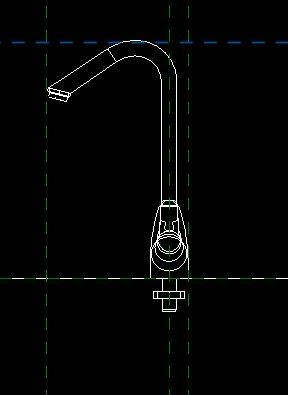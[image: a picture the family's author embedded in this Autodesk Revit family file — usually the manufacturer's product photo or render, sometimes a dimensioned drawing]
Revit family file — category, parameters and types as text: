
# Revit family: AV5030001_Grifería para Lavaplatos Sencillo Aluvia Palanca
name_source: partatom
category: Plumbing Fixtures
units: mm (PartAtom-declared; Revit-internal decimal feet)

## family parameters
Cut with Voids When Loaded = No
Host = Face
OmniClass Number = 23.45.55.14
OmniClass Title = Single Faucets
Part Type = Normal
Room Calculation Point = No
Round Connector Dimension = Use Diameter
Shared = No

## types (1)
- AV5030001_Grifería para Lavaplatos Sencillo Aluvia Palanca
    Alto = 333 mm  [stored 1.09252 ft]
    Ancho = 103 mm  [stored 0.337927 ft]
    Capacidad de flujo máximo a 60 psi = 5,7 L/min
    Default Elevation = 1219 mm
    Fabricante = Corona
    Garantia = 30 años
    Material = Corona_Plastico_Cromado
    Normatividad NTC 1644 = SI
    Peso Neto = 282 gr. - 0,62 lb
    Profundidad = 200 mm  [stored 0.656168 ft]
    Temperatura de uso = 5ºC a 71ºC
    URL = https://corona.co
    Vida útil o desgaste (pico) = 50.000 ciclos
    Vida útil o desgaste (unidad) = 500.000 ciclos

note: [stored X ft] marks values corroborated as IEEE doubles in the binary element streams (Revit-internal decimal feet)

## geometry (parser evidence)
native form markers: Sweep x5
no freeform markers — native parametric forms only
